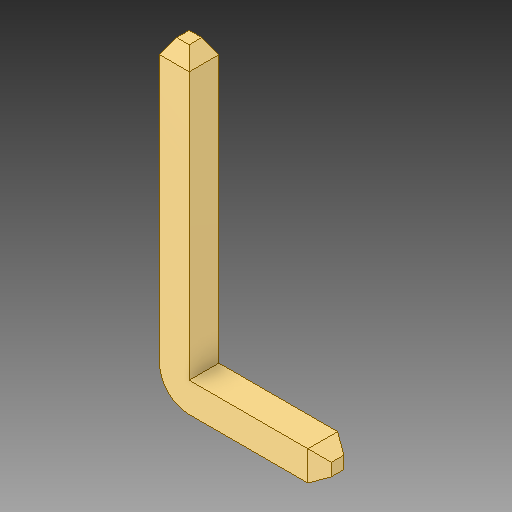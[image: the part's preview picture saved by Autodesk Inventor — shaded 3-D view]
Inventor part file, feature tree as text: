
AUTODESK INVENTOR PART (.ipt)
format: ipt  version: 2018 (Build 220112000, 112)  size: 87,040 bytes
history: native  units: mm
features: chamfer x1
ambient origin geometry x8: Origin, YZ Plane, XZ Plane, XY Plane, X Axis, Y Axis, Z Axis, Center Point
bodies: Solid1 (feature_tree)
feature tree (1):
  chamfer  "Chamfer2"  [1 undecoded]
note: 1 required parameter value undecoded (feature->parameter linkage not recoverable at this tier; creation-order binding heuristic only, values carry confidence <= 0.55)
